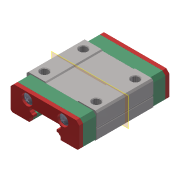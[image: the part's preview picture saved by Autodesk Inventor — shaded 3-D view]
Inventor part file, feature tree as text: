
AUTODESK INVENTOR PART (.ipt)
format: ipt  version: 2019.4 (Build 234330000, 330)  size: 484,864 bytes
history: imported  units: mm
features: other x9, plane x1, imported_body x1
ambient origin geometry x8: Origin, YZ Plane, XZ Plane, XY Plane, X Axis, Y Axis, Z Axis, Center Point
bodies: Solid1 (imported_parasolid), Solid2 (imported_parasolid), Solid3 (imported_parasolid), Solid4 (imported_parasolid), Solid5 (imported_parasolid), Solid6 (imported_parasolid), Solid7 (imported_parasolid), Solid8 (imported_parasolid), Solid9 (imported_parasolid)
feature tree (11):
  plane  "Work Plane1"
  other  "MID BODY, MGN 12C, LINEAR GUIDE BLOCK-1-solid1"
  other  "MID BODY, MGN 12C, LINEAR GUIDE BLOCK-1-solid2"
  other  "MID BODY, MGN 12C, LINEAR GUIDE BLOCK-1-solid3"
  other  "MID BODY, MGN 12C, LINEAR GUIDE BLOCK-1-solid4"
  other  "MID BODY, MGN 12C, LINEAR GUIDE BLOCK-1-solid5"
  other  "SCREW HEAD, MGN 12C, LINEAR GUIDE BLOCK-1-solid1"
  other  "SCREW HEAD, MGN 12C, LINEAR GUIDE BLOCK-2-solid1"
  other  "SCREW HEAD, MGN 12C, LINEAR GUIDE BLOCK-3-solid1"
  other  "SCREW HEAD, MGN 12C, LINEAR GUIDE BLOCK-4-solid1"
  imported_body  NMx_Import_Brep_tag  [imported B-rep: ~50 faces, bbox_mm=[19.044812, 8.226555, 21.7]]
